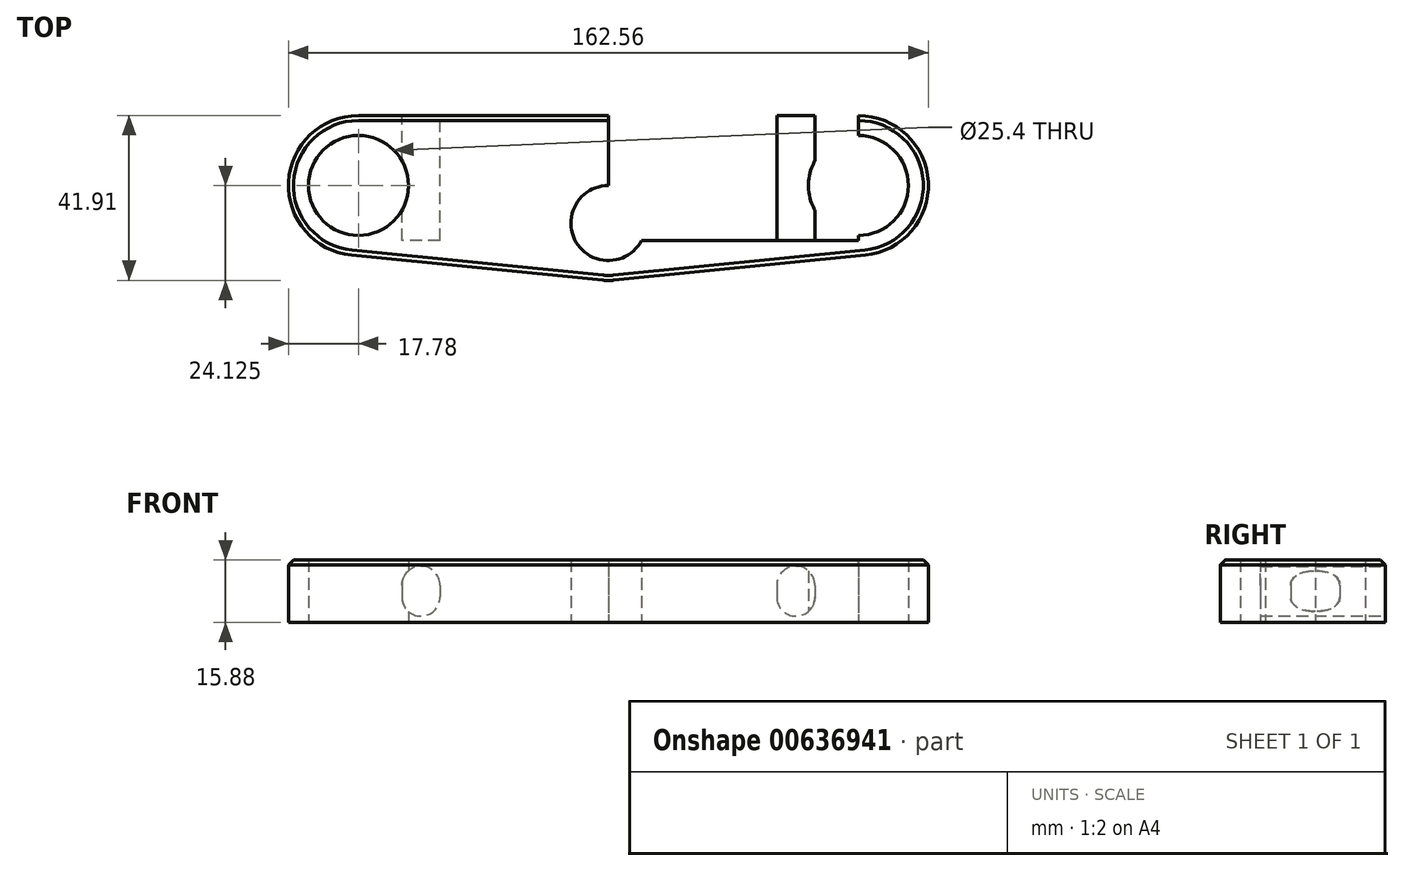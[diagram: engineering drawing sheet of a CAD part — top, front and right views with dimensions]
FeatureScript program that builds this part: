
annotation { "Feature Type Name" : "Feature", "Feature Type Description" : "" }
export const myFeature = defineFeature(function(context is Context, id is Id, definition is map)
    precondition{}
    {
        {
            var Q0;
            Q0=qCreatedBy(makeId("Top.planeOp"),FACE);
            var sketch = newSketch(context, id + "F0", { "sketchPlane" : qUnion([Q0])});
            skCircle(sketch, "E0", {"center": v(0, 0) * mm, "radius": 9.53 * mm});
            skCircle(sketch, "E1", {"center": v(-63.5, 9.52) * mm, "radius": 12.7 * mm});
            skCircle(sketch, "E2", {"center": v(63.5, 9.53) * mm, "radius": 12.7 * mm});
            skArc(sketch, "E3", {"start": v(-63.5, 27.3) * mm, "mid": v(-81.26, 10.4) * mm, "end": v(-65.26, -8.17) * mm});
            skArc(sketch, "E4", {"start": v(-1.45, -14.53) * mm, "mid": v(0, -14.6) * mm, "end": v(1.45, -14.53) * mm});
            skArc(sketch, "E5", {"start": v(65.26, -8.17) * mm, "mid": v(81.26, 10.4) * mm, "end": v(63.5, 27.3) * mm});
            skLineSegment(sketch, "E6", {"start": v(-65.26, -8.17) * mm, "end": v(-1.45, -14.53) * mm});
            skLineSegment(sketch, "E7", {"start": v(1.45, -14.53) * mm, "end": v(65.26, -8.17) * mm});
            skLineSegment(sketch, "E8", {"start": v(-63.5, 27.3) * mm, "end": v(63.5, 27.3) * mm});
            skSolve(sketch);
        }
        {
            var Q0;
            Q0=makeQuery(id+"F0.imprint","IMPRINT",FACE,{"disambiguationData":[TD([[makeQuery(id+"F0.imprint","IMPRINT",EDGE,{"derivedFrom":sQuery(id+"F0.wireOp",EDGE,"E0")}),-1.0]])]});
            extrude(context, id + "F1", {"entities" : qUnion([Q0]), "depth" : 15.88 * mm, "offsetDistance" : 25.4 * mm});
        }
        {
            var Q0;
            Q0=makeQuery(id+"F1.opExtrude","SWEPT_FACE",FACE,{"disambiguationData":[OSD([sQuery(id+"F0.wireOp",EDGE,"E8")])]});
            var sketch = newSketch(context, id + "F2", { "sketchPlane" : qUnion([Q0])});
            skLineSegment(sketch, "E9.left", {"start": v(52.45, 9.45) * mm, "end": v(52.45, 6.43) * mm});
            skLineSegment(sketch, "E9.right", {"start": v(42.8, 9.45) * mm, "end": v(42.8, 6.43) * mm});
            skArc(sketch, "E10", {"start": v(42.8, 6.43) * mm, "mid": v(47.62, 1.6) * mm, "end": v(52.45, 6.43) * mm});
            skArc(sketch, "E11", {"start": v(52.45, 9.45) * mm, "mid": v(47.62, 14.27) * mm, "end": v(42.8, 9.45) * mm});
            skLineSegment(sketch, "E12", {"start": v(0, 15.88) * mm, "end": v(0, 0) * mm});
            skArc(sketch, "E13.MirrorCS", {"start": v(-52.45, 9.45) * mm, "mid": v(-47.62, 14.27) * mm, "end": v(-42.8, 9.45) * mm});
            skArc(sketch, "E14.MirrorCS", {"start": v(-42.8, 6.43) * mm, "mid": v(-47.62, 1.6) * mm, "end": v(-52.45, 6.43) * mm});
            skLineSegment(sketch, "E15.MirrorCS", {"start": v(-42.8, 9.45) * mm, "end": v(-42.8, 6.43) * mm});
            skLineSegment(sketch, "E16.MirrorCS", {"start": v(-52.45, 9.45) * mm, "end": v(-52.45, 6.43) * mm});
            skSolve(sketch);
        }
        {
            var Q0;
            Q0=makeQuery(id+"F2.imprint","IMPRINT",FACE,{"disambiguationData":[TD([[makeQuery(id+"F2.imprint","IMPRINT",EDGE,{"derivedFrom":sQuery(id+"F2.wireOp",EDGE,"E9.left")}),-1.0]])]});
            var Q1;
            Q1=makeQuery(id+"F2.imprint","IMPRINT",FACE,{"disambiguationData":[TD([[makeQuery(id+"F2.imprint","IMPRINT",EDGE,{"derivedFrom":sQuery(id+"F2.wireOp",EDGE,"E13.MirrorCS")}),-1.0]])]});
            extrude(context, id + "F3", {"entities" : qUnion([Q0, Q1]), "operationType" : NewBodyOperationType.REMOVE, "oppositeDirection" : true, "depth" : 31.75 * mm, "offsetDistance" : 25.4 * mm});
        }
        {
            var Q0;
            Q0=makeQuery(id+"F1.opExtrude","CAP_EDGE",EDGE,{"disambiguationData":[OSD([sQuery(id+"F0.wireOp",EDGE,"E3")])],"isStart":false});
            chamfer(context, id + "F4", {"entities" : qUnion([Q0]), "width" : 1.27 * mm, "tangentPropagation" : true});
        }
    });
